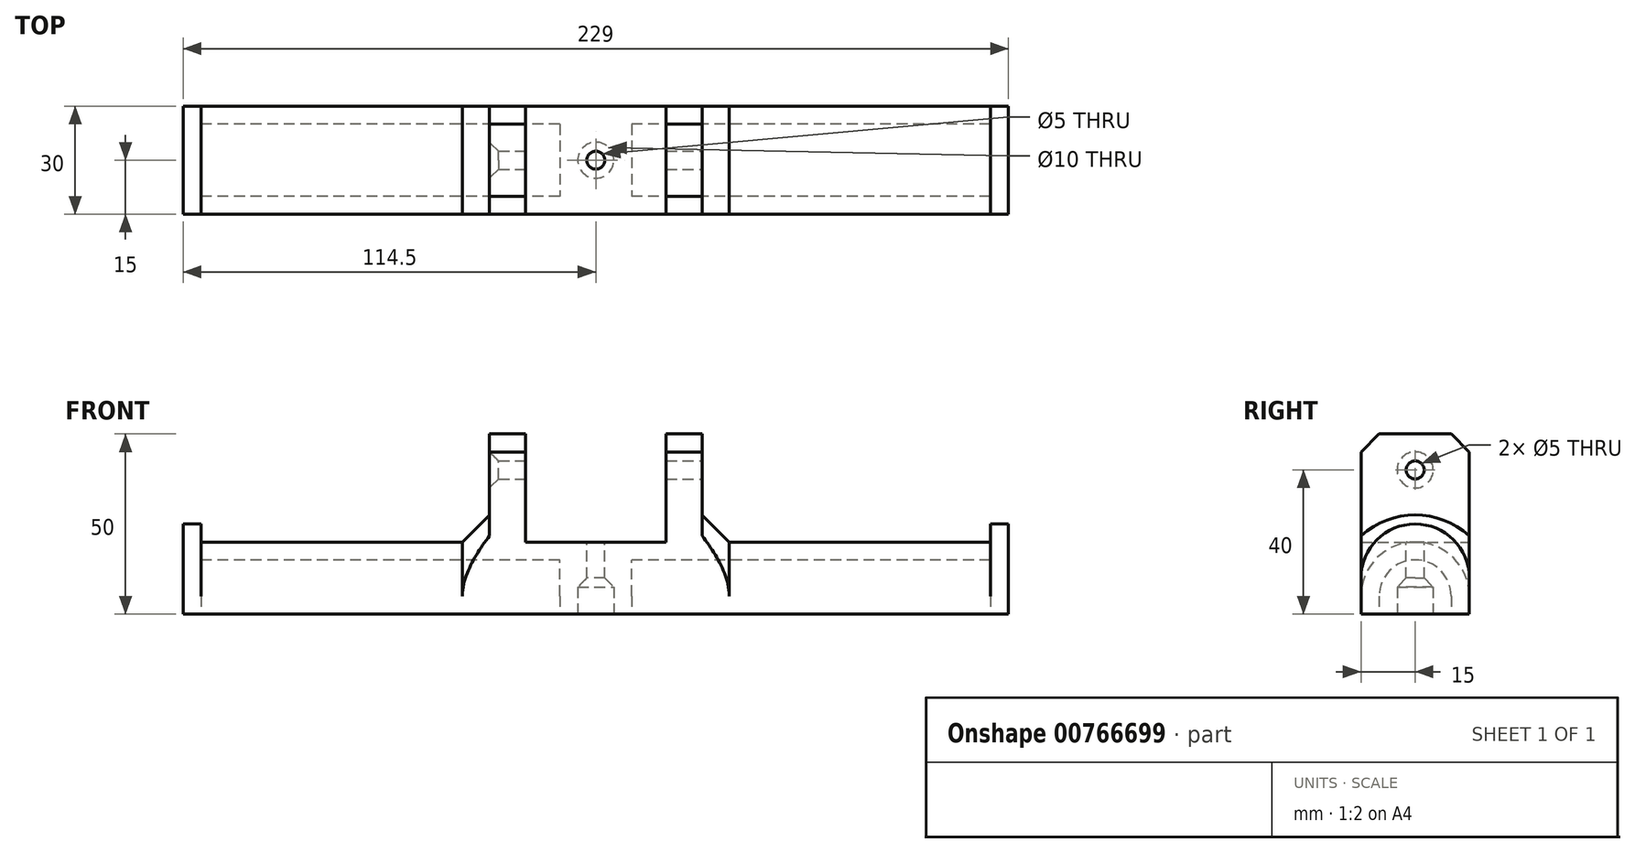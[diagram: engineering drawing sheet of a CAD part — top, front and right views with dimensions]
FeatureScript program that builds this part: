
annotation { "Feature Type Name" : "Feature", "Feature Type Description" : "" }
export const myFeature = defineFeature(function(context is Context, id is Id, definition is map)
    precondition{}
    {
        {
            var Q0;
            Q0=qCreatedBy(makeId("Front.planeOp"),FACE);
            var sketch = newSketch(context, id + "F0", { "sketchPlane" : qUnion([Q0])});
            skLineSegment(sketch, "E0", {"start": v(0, 0) * mm, "end": v(0, 100) * mm, "construction": true});
            skLineSegment(sketch, "E1", {"start": v(0, 0) * mm, "end": v(109.5, 0) * mm});
            skLineSegment(sketch, "E2", {"start": v(109.5, 0) * mm, "end": v(109.5, 20) * mm});
            skLineSegment(sketch, "E3", {"start": v(109.5, 20) * mm, "end": v(29.5, 20) * mm});
            skLineSegment(sketch, "E4", {"start": v(29.5, 20) * mm, "end": v(29.5, 50) * mm});
            skLineSegment(sketch, "E5", {"start": v(29.5, 50) * mm, "end": v(19.5, 50) * mm});
            skLineSegment(sketch, "E6", {"start": v(19.5, 50) * mm, "end": v(19.5, 20) * mm});
            skLineSegment(sketch, "E7", {"start": v(19.5, 20) * mm, "end": v(0, 20) * mm});
            skLineSegment(sketch, "E8.MirrorCS", {"start": v(0, 0) * mm, "end": v(-109.5, 0) * mm});
            skLineSegment(sketch, "E9.MirrorCS", {"start": v(-19.5, 20) * mm, "end": v(0, 20) * mm});
            skLineSegment(sketch, "E10.MirrorCS", {"start": v(-19.5, 50) * mm, "end": v(-19.5, 20) * mm});
            skLineSegment(sketch, "E11.MirrorCS", {"start": v(-109.5, 0) * mm, "end": v(-109.5, 20) * mm});
            skLineSegment(sketch, "E12.MirrorCS", {"start": v(-29.5, 20) * mm, "end": v(-29.5, 50) * mm});
            skLineSegment(sketch, "E13.MirrorCS", {"start": v(-29.5, 50) * mm, "end": v(-19.5, 50) * mm});
            skLineSegment(sketch, "E14.MirrorCS", {"start": v(-109.5, 20) * mm, "end": v(-29.5, 20) * mm});
            skSolve(sketch);
        }
        {
            var Q0;
            Q0=qSketchRegion(id+"F0",true);
            extrude(context, id + "F1", {"entities" : qUnion([Q0]), "depth" : 30 * mm, "offsetDistance" : 25 * mm});
        }
        {
            var Q0;
            Q0=makeQuery(id+"F1.opExtrude","CAP_EDGE",EDGE,{"disambiguationData":[OSD([sQuery(id+"F0.wireOp",EDGE,"E14.MirrorCS")])],"isStart":true});
            var Q1;
            Q1=makeQuery(id+"F1.opExtrude","CAP_EDGE",EDGE,{"disambiguationData":[OSD([sQuery(id+"F0.wireOp",EDGE,"E14.MirrorCS")])],"isStart":false});
            var Q2;
            Q2=makeQuery(id+"F1.opExtrude","CAP_EDGE",EDGE,{"disambiguationData":[OSD([sQuery(id+"F0.wireOp",EDGE,"E3")])],"isStart":true});
            var Q3;
            Q3=makeQuery(id+"F1.opExtrude","CAP_EDGE",EDGE,{"disambiguationData":[OSD([sQuery(id+"F0.wireOp",EDGE,"E3")])],"isStart":false});
            fillet(context, id + "F2", {"entities" : qUnion([Q0, Q1, Q2, Q3]), "radius" : 15 * mm, "tangentPropagation" : true, "allowEdgeOverflow" : false});
        }
        {
            var Q0;
            Q0=makeQuery(id+"F1.opExtrude","SWEPT_FACE",FACE,{"disambiguationData":[OSD([sQuery(id+"F0.wireOp",EDGE,"E11.MirrorCS")])]});
            var sketch = newSketch(context, id + "F3", { "sketchPlane" : qUnion([Q0])});
            skArc(sketch, "E15.0", {"start": v(25, 5) * mm, "mid": v(15, 15) * mm, "end": v(5, 5) * mm});
            skLineSegment(sketch, "E16.bottom", {"start": v(5, 5) * mm, "end": v(25, 5) * mm, "construction": true});
            skLineSegment(sketch, "E16.top", {"start": v(5, 0) * mm, "end": v(25, 0) * mm});
            skLineSegment(sketch, "E16.left", {"start": v(5, 5) * mm, "end": v(5, 0) * mm});
            skLineSegment(sketch, "E16.right", {"start": v(25, 5) * mm, "end": v(25, 0) * mm});
            skSolve(sketch);
        }
        {
            var Q0;
            Q0=qSketchRegion(id+"F3",true);
            extrude(context, id + "F4", {"entities" : qUnion([Q0]), "operationType" : NewBodyOperationType.REMOVE, "endBound" : BoundingType.THROUGH_ALL, "oppositeDirection" : true, "depth" : 25 * mm, "offsetDistance" : 25 * mm});
        }
        {
            var Q0;
            Q0=makeQuery(id+"F2.opFillet","BLEND_EDGE",EDGE,{"blendedFrom":[makeQuery(id+"F1.opExtrude","CAP_EDGE",EDGE,{"disambiguationData":[OSD([sQuery(id+"F0.wireOp",EDGE,"E14.MirrorCS")])],"isStart":true}),makeQuery(id+"F1.opExtrude","SWEPT_FACE",FACE,{"disambiguationData":[OSD([sQuery(id+"F0.wireOp",EDGE,"E12.MirrorCS")])]})],"blendedInto":[makeQuery(id+"F1.opExtrude","SWEPT_FACE",FACE,{"disambiguationData":[OSD([sQuery(id+"F0.wireOp",EDGE,"E12.MirrorCS")])]})]});
            var Q1;
            Q1=makeQuery(id+"F2.opFillet","BLEND_EDGE",EDGE,{"blendedFrom":[makeQuery(id+"F1.opExtrude","CAP_EDGE",EDGE,{"disambiguationData":[OSD([sQuery(id+"F0.wireOp",EDGE,"E3")])],"isStart":true}),makeQuery(id+"F1.opExtrude","SWEPT_FACE",FACE,{"disambiguationData":[OSD([sQuery(id+"F0.wireOp",EDGE,"E4")])]})],"blendedInto":[makeQuery(id+"F1.opExtrude","SWEPT_FACE",FACE,{"disambiguationData":[OSD([sQuery(id+"F0.wireOp",EDGE,"E4")])]})]});
            chamfer(context, id + "F5", {"entities" : qUnion([Q0, Q1]), "width" : 7.5 * mm, "tangentPropagation" : true});
        }
        {
            var Q0;
            Q0=makeQuery(id+"F1.opExtrude","CAP_EDGE",EDGE,{"disambiguationData":[OSD([sQuery(id+"F0.wireOp",EDGE,"E13.MirrorCS")])],"isStart":true});
            var Q1;
            Q1=makeQuery(id+"F1.opExtrude","CAP_EDGE",EDGE,{"disambiguationData":[OSD([sQuery(id+"F0.wireOp",EDGE,"E13.MirrorCS")])],"isStart":false});
            var Q2;
            Q2=makeQuery(id+"F1.opExtrude","CAP_EDGE",EDGE,{"disambiguationData":[OSD([sQuery(id+"F0.wireOp",EDGE,"E5")])],"isStart":true});
            var Q3;
            Q3=makeQuery(id+"F1.opExtrude","CAP_EDGE",EDGE,{"disambiguationData":[OSD([sQuery(id+"F0.wireOp",EDGE,"E5")])],"isStart":false});
            chamfer(context, id + "F6", {"entities" : qUnion([Q0, Q1, Q2, Q3]), "width" : 5 * mm, "tangentPropagation" : true});
        }
        {
            var Q0;
            Q0=makeQuery(id+"F1.opExtrude","SWEPT_FACE",FACE,{"disambiguationData":[OSD([sQuery(id+"F0.wireOp",EDGE,"E4")])]});
            var sketch = newSketch(context, id + "F7", { "sketchPlane" : qUnion([Q0])});
            skCircle(sketch, "E17", {"center": v(-15, 40) * mm, "radius": 2.5 * mm});
            skPoint(sketch, "E17.centerSnap0", {"position": v(-15, 50) * mm});
            skSolve(sketch);
        }
        {
            var Q0;
            Q0=qSketchRegion(id+"F7",true);
            extrude(context, id + "F8", {"entities" : qUnion([Q0]), "operationType" : NewBodyOperationType.REMOVE, "endBound" : BoundingType.THROUGH_ALL, "oppositeDirection" : true, "depth" : 25 * mm, "offsetDistance" : 25 * mm});
        }
        {
            var Q0;
            {var subQ1=sQuery(id+"F0.wireOp",EDGE,"E8.MirrorCS");var subQ3=sQuery(id+"F0.wireOp",EDGE,"E1");Q0=makeQuery(id+"F4.boolean.opBoolean","SPLIT",FACE,{"disambiguationData":[TD([makeQuery(id+"F4.opExtrude","SWEPT_FACE",FACE,{"disambiguationData":[OSD([sQuery(id+"F3.wireOp",EDGE,"E16.right")])]})])],"derivedFrom":makeQuery(id+"F1.opExtrude","SWEPT_FACE",FACE,{"disambiguationData":[OSD([subQ3,subQ1])]})});}
            var sketch = newSketch(context, id + "F9", { "sketchPlane" : qUnion([Q0])});
            skLineSegment(sketch, "E18.0.0", {"start": v(19.5, 0) * mm, "end": v(-19.5, 0) * mm, "construction": true});
            skLineSegment(sketch, "E18.0.1", {"start": v(-19.5, 0) * mm, "end": v(-19.5, 30) * mm, "construction": true});
            skLineSegment(sketch, "E18.0.2", {"start": v(-19.5, 30) * mm, "end": v(19.5, 30) * mm, "construction": true});
            skLineSegment(sketch, "E18.0.3", {"start": v(19.5, 30) * mm, "end": v(19.5, 0) * mm, "construction": true});
            skLineSegment(sketch, "E19.bottom", {"start": v(10, 5) * mm, "end": v(-10, 5) * mm});
            skLineSegment(sketch, "E19.top", {"start": v(10, 25) * mm, "end": v(-10, 25) * mm});
            skLineSegment(sketch, "E19.left", {"start": v(10, 5) * mm, "end": v(10, 25) * mm});
            skLineSegment(sketch, "E19.right", {"start": v(-10, 5) * mm, "end": v(-10, 25) * mm});
            skPoint(sketch, "E19.middle", {"position": v(0, 15) * mm});
            skSolve(sketch);
        }
        {
            var Q0;
            Q0=qSketchRegion(id+"F9",true);
            var Q1;
            Q1=makeQuery(id+"F4.boolean.opBoolean","COPY",FACE,{"derivedFrom":makeQuery(id+"F4.opExtrude","SWEPT_FACE",FACE,{"disambiguationData":[OSD([sQuery(id+"F3.wireOp",EDGE,"E15.0")])]})});
            extrude(context, id + "F10", {"entities" : qUnion([Q0]), "operationType" : NewBodyOperationType.ADD, "endBound" : BoundingType.UP_TO_SURFACE, "oppositeDirection" : true, "depth" : 25 * mm, "endBoundEntityFace" : qUnion([Q1]), "offsetDistance" : 25 * mm});
        }
        {
            var Q0;
            Q0=makeQuery(id+"F1.opExtrude","SWEPT_FACE",FACE,{"disambiguationData":[OSD([sQuery(id+"F0.wireOp",EDGE,"E7"),sQuery(id+"F0.wireOp",EDGE,"E9.MirrorCS")])]});
            var sketch = newSketch(context, id + "F11", { "sketchPlane" : qUnion([Q0])});
            skCircle(sketch, "E20", {"center": v(0, -15) * mm, "radius": 2.5 * mm});
            skPoint(sketch, "E20.centerSnap0", {"position": v(19.5, -15) * mm});
            skSolve(sketch);
        }
        {
            var Q0;
            Q0=qSketchRegion(id+"F11",true);
            extrude(context, id + "F12", {"entities" : qUnion([Q0]), "operationType" : NewBodyOperationType.REMOVE, "endBound" : BoundingType.THROUGH_ALL, "oppositeDirection" : true, "depth" : 25 * mm, "offsetDistance" : 25 * mm});
        }
        {
            var Q0;
            Q0=makeQuery(id+"F8.boolean.opBoolean","INTERSECT",EDGE,{"derivedFrom":[makeQuery(id+"F1.opExtrude","SWEPT_FACE",FACE,{"disambiguationData":[OSD([sQuery(id+"F0.wireOp",EDGE,"E12.MirrorCS")])]}),makeQuery(id+"F8.opExtrude","SWEPT_FACE",FACE,{"disambiguationData":[OSD([sQuery(id+"F7.wireOp",EDGE,"E17")])]})]});
            var Q1;
            Q1=makeQuery(id+"F8.boolean.opBoolean","COPY",EDGE,{"derivedFrom":makeQuery(id+"F8.opExtrude","CAP_EDGE",EDGE,{"disambiguationData":[OSD([sQuery(id+"F7.wireOp",EDGE,"E17")])],"isStart":true})});
            chamfer(context, id + "F13", {"entities" : qUnion([Q0, Q1]), "width" : 2.5 * mm, "tangentPropagation" : true});
        }
        {
            var Q0;
            Q0=makeQuery(id+"F1.opExtrude","CAP_FACE",FACE,{"disambiguationData":[OSD([sQuery(id+"F0.wireOp",EDGE,"E1"),sQuery(id+"F0.wireOp",EDGE,"E2"),sQuery(id+"F0.wireOp",EDGE,"E3"),sQuery(id+"F0.wireOp",EDGE,"E4"),sQuery(id+"F0.wireOp",EDGE,"E5"),sQuery(id+"F0.wireOp",EDGE,"E6"),sQuery(id+"F0.wireOp",EDGE,"E7"),sQuery(id+"F0.wireOp",EDGE,"E8.MirrorCS"),sQuery(id+"F0.wireOp",EDGE,"E9.MirrorCS"),sQuery(id+"F0.wireOp",EDGE,"E10.MirrorCS"),sQuery(id+"F0.wireOp",EDGE,"E11.MirrorCS"),sQuery(id+"F0.wireOp",EDGE,"E12.MirrorCS"),sQuery(id+"F0.wireOp",EDGE,"E13.MirrorCS"),sQuery(id+"F0.wireOp",EDGE,"E14.MirrorCS")])],"isStart":false});
            var sketch = newSketch(context, id + "F14", { "sketchPlane" : qUnion([Q0])});
            skLineSegment(sketch, "E21.bottom", {"start": v(-109.5, 0) * mm, "end": v(-114.5, 0) * mm});
            skLineSegment(sketch, "E21.top", {"start": v(-109.5, 25) * mm, "end": v(-114.5, 25) * mm});
            skLineSegment(sketch, "E21.left", {"start": v(-109.5, 0) * mm, "end": v(-109.5, 25) * mm});
            skLineSegment(sketch, "E21.right", {"start": v(-114.5, 0) * mm, "end": v(-114.5, 25) * mm});
            skLineSegment(sketch, "E22.bottom", {"start": v(109.5, 0) * mm, "end": v(114.5, 0) * mm});
            skLineSegment(sketch, "E22.top", {"start": v(109.5, 25) * mm, "end": v(114.5, 25) * mm});
            skLineSegment(sketch, "E22.left", {"start": v(109.5, 0) * mm, "end": v(109.5, 25) * mm});
            skLineSegment(sketch, "E22.right", {"start": v(114.5, 0) * mm, "end": v(114.5, 25) * mm});
            skSolve(sketch);
        }
        {
            var Q0;
            Q0=qSketchRegion(id+"F14",true);
            var Q1;
            Q1=makeQuery(id+"F1.opExtrude","CAP_FACE",FACE,{"disambiguationData":[OSD([sQuery(id+"F0.wireOp",EDGE,"E1"),sQuery(id+"F0.wireOp",EDGE,"E2"),sQuery(id+"F0.wireOp",EDGE,"E3"),sQuery(id+"F0.wireOp",EDGE,"E4"),sQuery(id+"F0.wireOp",EDGE,"E5"),sQuery(id+"F0.wireOp",EDGE,"E6"),sQuery(id+"F0.wireOp",EDGE,"E7"),sQuery(id+"F0.wireOp",EDGE,"E8.MirrorCS"),sQuery(id+"F0.wireOp",EDGE,"E9.MirrorCS"),sQuery(id+"F0.wireOp",EDGE,"E10.MirrorCS"),sQuery(id+"F0.wireOp",EDGE,"E11.MirrorCS"),sQuery(id+"F0.wireOp",EDGE,"E12.MirrorCS"),sQuery(id+"F0.wireOp",EDGE,"E13.MirrorCS"),sQuery(id+"F0.wireOp",EDGE,"E14.MirrorCS")])],"isStart":true});
            extrude(context, id + "F15", {"entities" : qUnion([Q0]), "operationType" : NewBodyOperationType.ADD, "endBound" : BoundingType.UP_TO_SURFACE, "oppositeDirection" : true, "depth" : 25 * mm, "endBoundEntityFace" : qUnion([Q1]), "offsetDistance" : 25 * mm});
        }
        {
            var Q0;
            Q0=makeQuery(id+"F15.opExtrude","CAP_EDGE",EDGE,{"disambiguationData":[OSD([sQuery(id+"F14.wireOp",EDGE,"E22.top")])],"isStart":false});
            var Q1;
            Q1=makeQuery(id+"F15.opExtrude","CAP_EDGE",EDGE,{"disambiguationData":[OSD([sQuery(id+"F14.wireOp",EDGE,"E22.top")])],"isStart":true});
            var Q2;
            Q2=makeQuery(id+"F15.opExtrude","CAP_EDGE",EDGE,{"disambiguationData":[OSD([sQuery(id+"F14.wireOp",EDGE,"E21.top")])],"isStart":true});
            var Q3;
            Q3=makeQuery(id+"F15.opExtrude","CAP_EDGE",EDGE,{"disambiguationData":[OSD([sQuery(id+"F14.wireOp",EDGE,"E21.top")])],"isStart":false});
            fillet(context, id + "F16", {"entities" : qUnion([Q0, Q1, Q2, Q3]), "radius" : 15 * mm, "tangentPropagation" : true, "allowEdgeOverflow" : false});
        }
        {
            var Q0;
            {var subQ6=sQuery(id+"F0.wireOp",EDGE,"E8.MirrorCS");var subQ13=sQuery(id+"F0.wireOp",EDGE,"E1");var subQ16=makeQuery(id+"F1.opExtrude","SWEPT_FACE",FACE,{"disambiguationData":[OSD([subQ13,subQ6])]});Q0=makeQuery(id+"F15.boolean.opBoolean","MERGE",FACE,{"derivedFrom":[makeQuery(id+"F10.boolean.opBoolean","MERGE",FACE,{"derivedFrom":[makeQuery(id+"F4.boolean.opBoolean","SPLIT",FACE,{"disambiguationData":[TD([makeQuery(id+"F4.opExtrude","SWEPT_FACE",FACE,{"disambiguationData":[OSD([sQuery(id+"F3.wireOp",EDGE,"E16.left")])]})])],"derivedFrom":subQ16}),makeQuery(id+"F4.boolean.opBoolean","SPLIT",FACE,{"disambiguationData":[TD([makeQuery(id+"F4.opExtrude","SWEPT_FACE",FACE,{"disambiguationData":[OSD([sQuery(id+"F3.wireOp",EDGE,"E16.right")])]})])],"derivedFrom":subQ16}),makeQuery(id+"F10.opExtrude","CAP_FACE",FACE,{"disambiguationData":[OSD([sQuery(id+"F9.wireOp",EDGE,"E19.bottom"),sQuery(id+"F9.wireOp",EDGE,"E19.top"),sQuery(id+"F9.wireOp",EDGE,"E19.left"),sQuery(id+"F9.wireOp",EDGE,"E19.right")])],"isStart":true})]}),makeQuery(id+"F15.opExtrude","SWEPT_FACE",FACE,{"disambiguationData":[OSD([sQuery(id+"F14.wireOp",EDGE,"E21.bottom")])]}),makeQuery(id+"F15.opExtrude","SWEPT_FACE",FACE,{"disambiguationData":[OSD([sQuery(id+"F14.wireOp",EDGE,"E22.bottom")])]})]});}
            var sketch = newSketch(context, id + "F17", { "sketchPlane" : qUnion([Q0])});
            skCircle(sketch, "E23", {"center": v(0, 15) * mm, "radius": 5 * mm});
            skSolve(sketch);
        }
        {
            var Q0;
            Q0=qSketchRegion(id+"F17",true);
            extrude(context, id + "F18", {"entities" : qUnion([Q0]), "operationType" : NewBodyOperationType.REMOVE, "oppositeDirection" : true, "depth" : 7.5 * mm, "offsetDistance" : 25 * mm});
        }
        {
            var Q0;
            Q0=makeQuery(id+"F18.boolean.opBoolean","INTERSECT",EDGE,{"derivedFrom":[makeQuery(id+"F12.boolean.opBoolean","COPY",FACE,{"derivedFrom":makeQuery(id+"F12.opExtrude","SWEPT_FACE",FACE,{"disambiguationData":[OSD([sQuery(id+"F11.wireOp",EDGE,"E20")])]})}),makeQuery(id+"F18.opExtrude","CAP_FACE",FACE,{"disambiguationData":[OSD([sQuery(id+"F17.wireOp",EDGE,"E23")])],"isStart":false})]});
            chamfer(context, id + "F19", {"entities" : qUnion([Q0]), "width" : 2.5 * mm, "tangentPropagation" : true});
        }
    });
